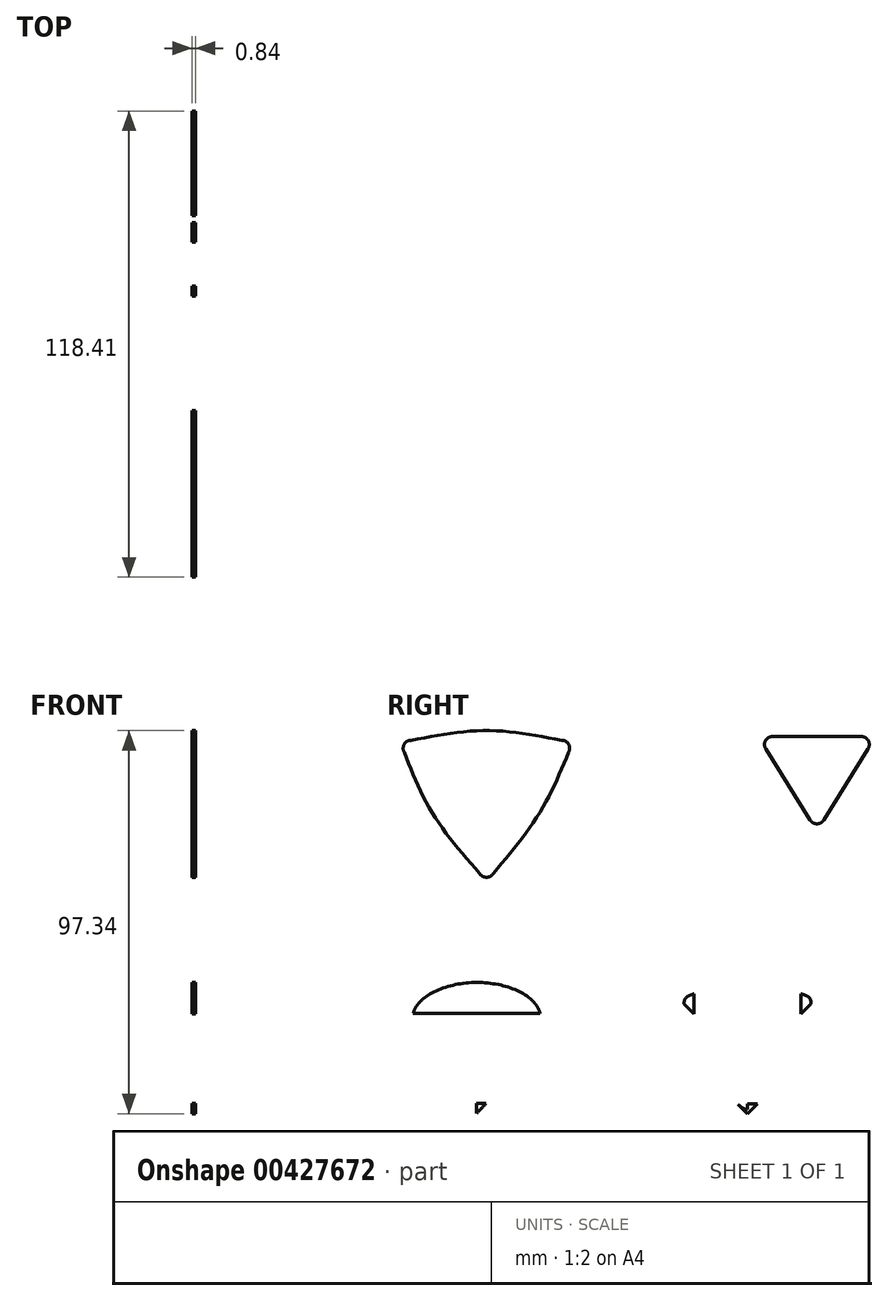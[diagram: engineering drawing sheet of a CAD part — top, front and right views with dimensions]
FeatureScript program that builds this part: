
annotation { "Feature Type Name" : "Feature", "Feature Type Description" : "" }
export const myFeature = defineFeature(function(context is Context, id is Id, definition is map)
    precondition{}
    {
        {
            var Q0;
            Q0=qCreatedBy(makeId("Right.planeOp"),FACE);
            var sketch = newSketch(context, id + "F0", { "sketchPlane" : qUnion([Q0])});
            skLineSegment(sketch, "E0", {"start": v(0, -11.07) * mm, "end": v(0, -44.35) * mm});
            skLineSegment(sketch, "E1", {"start": v(0, -44.35) * mm, "end": v(32.26, -44.35) * mm});
            skPoint(sketch, "E2", {"position": v(16.13, -44.35) * mm});
            skLineSegment(sketch, "E3", {"start": v(0, -11.07) * mm, "end": v(32.26, -11.07) * mm});
            skLineSegment(sketch, "E4", {"start": v(32.26, -11.07) * mm, "end": v(32.26, -44.35) * mm});
            skPoint(sketch, "E5", {"position": v(0, -16.42) * mm});
            skPoint(sketch, "E6", {"position": v(32.26, -16.42) * mm});
            skLineSegment(sketch, "E7", {"start": v(16.13, -44.35) * mm, "end": v(16.13, -39.27) * mm});
            skLineSegment(sketch, "E8", {"start": v(16.13, -41.8) * mm, "end": v(13.59, -41.8) * mm});
            skLineSegment(sketch, "E9", {"start": v(13.59, -41.8) * mm, "end": v(16.13, -41.8) * mm});
            skLineSegment(sketch, "E10", {"start": v(18.67, -41.8) * mm, "end": v(16.13, -41.8) * mm});
            skLineSegment(sketch, "E11", {"start": v(16.13, -44.35) * mm, "end": v(13.59, -41.8) * mm});
            skLineSegment(sketch, "E12", {"start": v(16.13, -44.35) * mm, "end": v(18.67, -41.8) * mm});
            skLineSegment(sketch, "E13", {"start": v(0, -16.42) * mm, "end": v(2.54, -16.42) * mm});
            skLineSegment(sketch, "E14", {"start": v(2.54, -16.42) * mm, "end": v(2.54, -13.88) * mm});
            skLineSegment(sketch, "E15", {"start": v(2.54, -13.88) * mm, "end": v(2.54, -16.42) * mm});
            skLineSegment(sketch, "E16", {"start": v(2.54, -18.96) * mm, "end": v(2.54, -16.42) * mm});
            skLineSegment(sketch, "E17", {"start": v(0, -16.42) * mm, "end": v(2.54, -18.96) * mm});
            skLineSegment(sketch, "E18", {"start": v(2.54, -13.88) * mm, "end": v(0, -16.42) * mm});
            skLineSegment(sketch, "E19", {"start": v(32.26, -16.42) * mm, "end": v(29.72, -16.42) * mm});
            skLineSegment(sketch, "E20", {"start": v(29.72, -16.42) * mm, "end": v(29.72, -13.88) * mm});
            skLineSegment(sketch, "E21", {"start": v(29.72, -13.88) * mm, "end": v(29.72, -16.42) * mm});
            skLineSegment(sketch, "E22", {"start": v(29.72, -18.96) * mm, "end": v(29.72, -16.42) * mm});
            skLineSegment(sketch, "E23", {"start": v(29.72, -18.96) * mm, "end": v(32.26, -16.42) * mm});
            skFitSpline(sketch, "E24", {"points": [v(2.54, -13.88) * mm, v(16.13, -11.07) * mm, v(29.72, -13.88) * mm, v(32.26, -16.42) * mm, v(18.67, -41.8) * mm, v(13.59, -41.8) * mm, v(0, -16.42) * mm, v(2.54, -13.88) * mm]});
            skLineSegment(sketch, "E25", {"start": v(29.72, -13.88) * mm, "end": v(32.26, -16.42) * mm});
            skSolve(sketch);
        }
        {
            var Q0;
            {var subQ0=sQuery(id+"F0.wireOp",EDGE,"E24");var subQ1=sQuery(id+"F0.wireOp",EDGE,"E0");var subQ3=makeQuery(id+"F0.imprint","INTERSECT",VERTEX,{"derivedFrom":[subQ1,subQ0]});Q0=makeQuery(id+"F0.imprint","IMPRINT",FACE,{"disambiguationData":[TD([[makeQuery(id+"F0.imprint","IMPRINT",EDGE,{"disambiguationData":[TD([[subQ3,-1.0]])],"derivedFrom":subQ1}),-1.0]])]});}
            var Q1;
            {var subQ0=sQuery(id+"F0.wireOp",EDGE,"E24");var subQ1=sQuery(id+"F0.wireOp",EDGE,"E4");var subQ3=makeQuery(id+"F0.imprint","INTERSECT",VERTEX,{"derivedFrom":[subQ1,subQ0]});Q1=makeQuery(id+"F0.imprint","IMPRINT",FACE,{"disambiguationData":[TD([[makeQuery(id+"F0.imprint","IMPRINT",EDGE,{"disambiguationData":[TD([[subQ3,-1.0]])],"derivedFrom":subQ1}),1.0]])]});}
            var Q2;
            Q2=makeQuery(id+"F0.imprint","IMPRINT",FACE,{"disambiguationData":[TD([[makeQuery(id+"F0.imprint","IMPRINT",EDGE,{"derivedFrom":sQuery(id+"F0.wireOp",EDGE,"E13")}),-1.0]])]});
            var Q3;
            Q3=makeQuery(id+"F0.imprint","IMPRINT",FACE,{"disambiguationData":[TD([[makeQuery(id+"F0.imprint","IMPRINT",EDGE,{"derivedFrom":sQuery(id+"F0.wireOp",EDGE,"E19")}),1.0]])]});
            var Q4;
            {var subQ1=sQuery(id+"F0.wireOp",EDGE,"E18");Q4=makeQuery(id+"F0.imprint","IMPRINT",FACE,{"disambiguationData":[TD([[makeQuery(id+"F0.imprint","IMPRINT",EDGE,{"derivedFrom":subQ1}),-1.0]])]});}
            var Q5;
            {var subQ0=sQuery(id+"F0.wireOp",EDGE,"E25");Q5=makeQuery(id+"F0.imprint","IMPRINT",FACE,{"disambiguationData":[TD([[makeQuery(id+"F0.imprint","IMPRINT",EDGE,{"derivedFrom":subQ0}),1.0]])]});}
            var Q6;
            {var subQ1=sQuery(id+"F0.wireOp",EDGE,"E7");var subQ3=sQuery(id+"F0.wireOp",EDGE,"E24");var subQ4=makeQuery(id+"F0.imprint","INTERSECT",VERTEX,{"derivedFrom":[subQ1,subQ3]});Q6=makeQuery(id+"F0.imprint","IMPRINT",FACE,{"disambiguationData":[TD([[makeQuery(id+"F0.imprint","IMPRINT",EDGE,{"disambiguationData":[TD([[subQ4,-1.0]])],"derivedFrom":subQ3}),1.0]])]});}
            var Q7;
            {var subQ1=sQuery(id+"F0.wireOp",EDGE,"E7");var subQ3=sQuery(id+"F0.wireOp",EDGE,"E24");var subQ4=makeQuery(id+"F0.imprint","INTERSECT",VERTEX,{"derivedFrom":[subQ1,subQ3]});Q7=makeQuery(id+"F0.imprint","IMPRINT",FACE,{"disambiguationData":[TD([[makeQuery(id+"F0.imprint","IMPRINT",EDGE,{"disambiguationData":[TD([[subQ4,1.0]])],"derivedFrom":subQ3}),1.0]])]});}
            var Q8;
            Q8=makeQuery(id+"F0.imprint","IMPRINT",FACE,{"disambiguationData":[TD([[makeQuery(id+"F0.imprint","IMPRINT",EDGE,{"derivedFrom":sQuery(id+"F0.wireOp",EDGE,"E13")}),1.0]])]});
            var Q9;
            Q9=makeQuery(id+"F0.imprint","IMPRINT",FACE,{"disambiguationData":[TD([[makeQuery(id+"F0.imprint","IMPRINT",EDGE,{"derivedFrom":sQuery(id+"F0.wireOp",EDGE,"E19")}),-1.0]])]});
            var Q10;
            {var subQ8=sQuery(id+"F0.wireOp",EDGE,"E9");Q10=makeQuery(id+"F0.imprint","IMPRINT",FACE,{"disambiguationData":[TD([[makeQuery(id+"F0.imprint","IMPRINT",EDGE,{"derivedFrom":subQ8}),1.0]])]});}
            var Q11;
            {var subQ0=sQuery(id+"F0.wireOp",EDGE,"E9");Q11=makeQuery(id+"F0.imprint","IMPRINT",FACE,{"disambiguationData":[TD([[makeQuery(id+"F0.imprint","IMPRINT",EDGE,{"derivedFrom":subQ0}),-1.0]])]});}
            var Q12;
            {var subQ0=sQuery(id+"F0.wireOp",EDGE,"E10");Q12=makeQuery(id+"F0.imprint","IMPRINT",FACE,{"disambiguationData":[TD([[makeQuery(id+"F0.imprint","IMPRINT",EDGE,{"derivedFrom":subQ0}),1.0]])]});}
            extrude(context, id + "F1", {"entities" : qUnion([Q0, Q1, Q2, Q3, Q4, Q5, Q6, Q7, Q8, Q9, Q10, Q11, Q12]), "depth" : 0.84 * mm});
        }
        {
            var Q0;
            Q0=qCreatedBy(makeId("Right.planeOp"),FACE);
            var sketch = newSketch(context, id + "F2", { "sketchPlane" : qUnion([Q0])});
            skLineSegment(sketch, "E26", {"start": v(-68.83, -11.02) * mm, "end": v(-68.83, -44.3) * mm});
            skLineSegment(sketch, "E27", {"start": v(-68.83, -44.3) * mm, "end": v(-36.58, -44.3) * mm});
            skPoint(sketch, "E28", {"position": v(-52.7, -44.3) * mm});
            skLineSegment(sketch, "E29", {"start": v(-68.83, -11.02) * mm, "end": v(-36.58, -11.02) * mm});
            skLineSegment(sketch, "E30", {"start": v(-36.58, -11.02) * mm, "end": v(-36.58, -44.3) * mm});
            skPoint(sketch, "E31", {"position": v(-68.83, -16.36) * mm});
            skPoint(sketch, "E32", {"position": v(-36.58, -16.36) * mm});
            skLineSegment(sketch, "E33", {"start": v(-52.7, -44.3) * mm, "end": v(-52.7, -39.21) * mm});
            skLineSegment(sketch, "E34", {"start": v(-52.7, -41.75) * mm, "end": v(-55.24, -41.75) * mm});
            skLineSegment(sketch, "E35", {"start": v(-55.24, -41.75) * mm, "end": v(-52.7, -41.75) * mm});
            skLineSegment(sketch, "E36", {"start": v(-50.16, -41.75) * mm, "end": v(-52.7, -41.75) * mm});
            skLineSegment(sketch, "E37", {"start": v(-52.7, -44.3) * mm, "end": v(-55.24, -41.75) * mm});
            skLineSegment(sketch, "E38", {"start": v(-52.7, -44.3) * mm, "end": v(-50.16, -41.75) * mm});
            skLineSegment(sketch, "E39", {"start": v(-68.83, -16.36) * mm, "end": v(-66.3, -16.36) * mm});
            skLineSegment(sketch, "E40", {"start": v(-66.3, -16.36) * mm, "end": v(-66.3, -13.82) * mm});
            skLineSegment(sketch, "E41", {"start": v(-66.3, -13.82) * mm, "end": v(-66.3, -16.36) * mm});
            skLineSegment(sketch, "E42", {"start": v(-66.3, -18.9) * mm, "end": v(-66.3, -16.36) * mm});
            skLineSegment(sketch, "E43", {"start": v(-68.83, -16.36) * mm, "end": v(-66.3, -18.9) * mm});
            skLineSegment(sketch, "E44", {"start": v(-66.3, -13.82) * mm, "end": v(-68.83, -16.36) * mm});
            skLineSegment(sketch, "E45", {"start": v(-36.58, -16.36) * mm, "end": v(-39.12, -16.36) * mm});
            skLineSegment(sketch, "E46", {"start": v(-39.12, -16.36) * mm, "end": v(-39.12, -13.82) * mm});
            skLineSegment(sketch, "E47", {"start": v(-39.12, -13.82) * mm, "end": v(-39.12, -16.36) * mm});
            skLineSegment(sketch, "E48", {"start": v(-39.12, -18.9) * mm, "end": v(-39.12, -16.36) * mm});
            skLineSegment(sketch, "E49", {"start": v(-39.12, -18.9) * mm, "end": v(-36.58, -16.36) * mm});
            skLineSegment(sketch, "E50", {"start": v(-39.12, -13.82) * mm, "end": v(-36.58, -16.36) * mm});
            skLineSegment(sketch, "E51", {"start": v(-66.3, -18.9) * mm, "end": v(-68.83, -18.9) * mm});
            skLineSegment(sketch, "E52", {"start": v(-68.83, -18.9) * mm, "end": v(-36.58, -18.9) * mm});
            skFitSpline(sketch, "E53", {"points": [v(-55.24, -41.75) * mm, v(-68.83, -18.9) * mm, v(-52.7, -11.02) * mm, v(-36.58, -18.9) * mm, v(-52.7, -44.3) * mm], "startDerivative": vector(-84.15, 94.44) * mm, "endDerivative": vector(-92.62, -99.56) * mm});
            skSolve(sketch);
        }
        {
            var Q0;
            {var subQ0=sQuery(id+"F2.wireOp",EDGE,"E35");Q0=makeQuery(id+"F2.imprint","IMPRINT",FACE,{"disambiguationData":[TD([[makeQuery(id+"F2.imprint","IMPRINT",EDGE,{"derivedFrom":subQ0}),1.0]])]});}
            var Q1;
            {var subQ4=sQuery(id+"F2.wireOp",EDGE,"E42");Q1=makeQuery(id+"F2.imprint","IMPRINT",FACE,{"disambiguationData":[TD([[makeQuery(id+"F2.imprint","IMPRINT",EDGE,{"derivedFrom":subQ4}),-1.0]])]});}
            var Q2;
            {var subQ1=sQuery(id+"F2.wireOp",EDGE,"E43");var subQ3=sQuery(id+"F2.wireOp",EDGE,"E53");var subQ4=makeQuery(id+"F2.imprint","INTERSECT",VERTEX,{"derivedFrom":[subQ1,subQ3]});Q2=makeQuery(id+"F2.imprint","IMPRINT",FACE,{"disambiguationData":[TD([[makeQuery(id+"F2.imprint","IMPRINT",EDGE,{"disambiguationData":[TD([[subQ4,-1.0]])],"derivedFrom":subQ1}),-1.0]])]});}
            var Q3;
            {var subQ0=sQuery(id+"F2.wireOp",EDGE,"E42");Q3=makeQuery(id+"F2.imprint","IMPRINT",FACE,{"disambiguationData":[TD([[makeQuery(id+"F2.imprint","IMPRINT",EDGE,{"derivedFrom":subQ0}),1.0]])]});}
            var Q4;
            {var subQ1=sQuery(id+"F2.wireOp",EDGE,"E39");var subQ3=sQuery(id+"F2.wireOp",EDGE,"E53");var subQ4=makeQuery(id+"F2.imprint","INTERSECT",VERTEX,{"derivedFrom":[subQ1,subQ3]});Q4=makeQuery(id+"F2.imprint","IMPRINT",FACE,{"disambiguationData":[TD([[makeQuery(id+"F2.imprint","IMPRINT",EDGE,{"disambiguationData":[TD([[subQ4,-1.0]])],"derivedFrom":subQ3}),-1.0]])]});}
            var Q5;
            {var subQ1=sQuery(id+"F2.wireOp",EDGE,"E49");var subQ3=sQuery(id+"F2.wireOp",EDGE,"E53");var subQ4=makeQuery(id+"F2.imprint","INTERSECT",VERTEX,{"derivedFrom":[subQ1,subQ3]});Q5=makeQuery(id+"F2.imprint","IMPRINT",FACE,{"disambiguationData":[TD([[makeQuery(id+"F2.imprint","IMPRINT",EDGE,{"disambiguationData":[TD([[subQ4,1.0]])],"derivedFrom":subQ1}),-1.0]])]});}
            var Q6;
            {var subQ0=sQuery(id+"F2.wireOp",EDGE,"E48");Q6=makeQuery(id+"F2.imprint","IMPRINT",FACE,{"disambiguationData":[TD([[makeQuery(id+"F2.imprint","IMPRINT",EDGE,{"derivedFrom":subQ0}),-1.0]])]});}
            var Q7;
            {var subQ0=sQuery(id+"F2.wireOp",EDGE,"E53");var subQ3=sQuery(id+"F2.wireOp",EDGE,"E36");var subQ5=makeQuery(id+"F2.imprint","INTERSECT",VERTEX,{"derivedFrom":[subQ3,subQ0]});Q7=makeQuery(id+"F2.imprint","IMPRINT",FACE,{"disambiguationData":[TD([[makeQuery(id+"F2.imprint","IMPRINT",EDGE,{"disambiguationData":[TD([[subQ5,-1.0]])],"derivedFrom":subQ3}),1.0]])]});}
            var Q8;
            {var subQ2=sQuery(id+"F2.wireOp",EDGE,"E35");Q8=makeQuery(id+"F2.imprint","IMPRINT",FACE,{"disambiguationData":[TD([[makeQuery(id+"F2.imprint","IMPRINT",EDGE,{"derivedFrom":subQ2}),-1.0]])]});}
            var Q9;
            {var subQ1=sQuery(id+"F2.wireOp",EDGE,"E45");var subQ3=sQuery(id+"F2.wireOp",EDGE,"E53");var subQ4=makeQuery(id+"F2.imprint","INTERSECT",VERTEX,{"derivedFrom":[subQ1,subQ3]});Q9=makeQuery(id+"F2.imprint","IMPRINT",FACE,{"disambiguationData":[TD([[makeQuery(id+"F2.imprint","IMPRINT",EDGE,{"disambiguationData":[TD([[subQ4,1.0]])],"derivedFrom":subQ3}),-1.0]])]});}
            extrude(context, id + "F3", {"entities" : qUnion([Q0, Q1, Q2, Q3, Q4, Q5, Q6, Q7, Q8, Q9]), "depth" : 0.84 * mm});
        }
        {
            var Q0;
            Q0=qCreatedBy(makeId("Right.planeOp"),FACE);
            var sketch = newSketch(context, id + "F4", { "sketchPlane" : qUnion([Q0])});
            skCircle(sketch, "E54", {"center": v(33.74, 44.11) * mm, "radius": 16.64 * mm});
            skLineSegment(sketch, "E55", {"start": v(18.82, 51.46) * mm, "end": v(33.74, 27.47) * mm});
            skLineSegment(sketch, "E56", {"start": v(33.74, 27.47) * mm, "end": v(48.67, 51.46) * mm});
            skLineSegment(sketch, "E57", {"start": v(48.67, 51.46) * mm, "end": v(18.82, 51.46) * mm});
            skSolve(sketch);
        }
        {
            var Q0;
            Q0=makeQuery(id+"F4.imprint","IMPRINT",FACE,{"disambiguationData":[TD([[makeQuery(id+"F4.imprint","IMPRINT",EDGE,{"derivedFrom":sQuery(id+"F4.wireOp",EDGE,"E55")}),1.0]])]});
            extrude(context, id + "F5", {"entities" : qUnion([Q0]), "depth" : 0.84 * mm});
        }
        {
            var Q0;
            Q0=makeQuery(id+"F5.opExtrude","SWEPT_EDGE",EDGE,{"disambiguationData":[OSD([sQuery(id+"F4.wireOp",EDGE,"E54"),sQuery(id+"F4.wireOp",EDGE,"E55"),sQuery(id+"F4.wireOp",EDGE,"E57")])]});
            var Q1;
            Q1=makeQuery(id+"F5.opExtrude","SWEPT_EDGE",EDGE,{"disambiguationData":[OSD([sQuery(id+"F4.wireOp",EDGE,"E54"),sQuery(id+"F4.wireOp",EDGE,"E55"),sQuery(id+"F4.wireOp",EDGE,"E56")])]});
            var Q2;
            Q2=makeQuery(id+"F5.opExtrude","SWEPT_EDGE",EDGE,{"disambiguationData":[OSD([sQuery(id+"F4.wireOp",EDGE,"E54"),sQuery(id+"F4.wireOp",EDGE,"E56"),sQuery(id+"F4.wireOp",EDGE,"E57")])]});
            fillet(context, id + "F6", {"entities" : qUnion([Q0, Q1, Q2]), "radius" : 2.03 * mm, "tangentPropagation" : true, "allowEdgeOverflow" : false});
        }
        {
            var Q0;
            Q0=qCreatedBy(makeId("Right.planeOp"),FACE);
            var sketch = newSketch(context, id + "F7", { "sketchPlane" : qUnion([Q0])});
            skCircle(sketch, "E58", {"center": v(-50.21, 39.29) * mm, "radius": 25.4 * mm});
            skLineSegment(sketch, "E59", {"start": v(-73, 50.52) * mm, "end": v(-50.21, 13.89) * mm});
            skLineSegment(sketch, "E60", {"start": v(-50.21, 13.89) * mm, "end": v(-27.43, 50.52) * mm});
            skLineSegment(sketch, "E61", {"start": v(-27.43, 50.52) * mm, "end": v(-73, 50.52) * mm});
            skSolve(sketch);
        }
        {
            var Q0;
            Q0=makeQuery(id+"F7.imprint","IMPRINT",FACE,{"disambiguationData":[TD([[makeQuery(id+"F7.imprint","IMPRINT",EDGE,{"derivedFrom":sQuery(id+"F7.wireOp",EDGE,"E59")}),1.0]])]});
            extrude(context, id + "F8", {"entities" : qUnion([Q0]), "depth" : 0.84 * mm});
        }
        {
            var Q0;
            Q0=makeQuery(id+"F8.opExtrude","SWEPT_EDGE",EDGE,{"disambiguationData":[OSD([sQuery(id+"F7.wireOp",EDGE,"E58"),sQuery(id+"F7.wireOp",EDGE,"E59"),sQuery(id+"F7.wireOp",EDGE,"E61")])]});
            var Q1;
            Q1=makeQuery(id+"F8.opExtrude","SWEPT_EDGE",EDGE,{"disambiguationData":[OSD([sQuery(id+"F7.wireOp",EDGE,"E58"),sQuery(id+"F7.wireOp",EDGE,"E60"),sQuery(id+"F7.wireOp",EDGE,"E61")])]});
            var Q2;
            Q2=makeQuery(id+"F8.opExtrude","SWEPT_EDGE",EDGE,{"disambiguationData":[OSD([sQuery(id+"F7.wireOp",EDGE,"E58"),sQuery(id+"F7.wireOp",EDGE,"E59"),sQuery(id+"F7.wireOp",EDGE,"E60")])]});
            fillet(context, id + "F9", {"entities" : qUnion([Q0, Q1, Q2]), "radius" : 2.03 * mm, "tangentPropagation" : true, "allowEdgeOverflow" : false});
        }
        {
            var Q0;
            Q0=makeQuery(id+"F8.opExtrude","CAP_FACE",FACE,{"disambiguationData":[OSD([sQuery(id+"F7.wireOp",EDGE,"E59"),sQuery(id+"F7.wireOp",EDGE,"E60"),sQuery(id+"F7.wireOp",EDGE,"E61")])],"isStart":false});
            var sketch = newSketch(context, id + "F10", { "sketchPlane" : qUnion([Q0])});
            skPoint(sketch, "E62.1.internal.snap0", {"position": v(-50.21, 50.52) * mm});
            skFitSpline(sketch, "E62", {"points": [v(-69.34, 50.52) * mm, v(-50.21, 52.99) * mm, v(-31.09, 50.52) * mm], "startDerivative": vector(38.25, 7.42) * mm, "endDerivative": vector(38.25, -7.42) * mm});
            skPoint(sketch, "E63.1.internal.snap0", {"position": v(-38.93, 32.04) * mm});
            skFitSpline(sketch, "E63", {"points": [v(-29.36, 47.41) * mm, v(-36.73, 32.04) * mm, v(-48.49, 16.66) * mm], "startDerivative": vector(-13.4, -32.23) * mm, "endDerivative": vector(-24.74, -29.3) * mm});
            skPoint(sketch, "E64.1.internal.snap0", {"position": v(-61.5, 32.04) * mm});
            skFitSpline(sketch, "E64", {"points": [v(-51.94, 16.66) * mm, v(-63.97, 32.04) * mm, v(-71.07, 47.41) * mm], "startDerivative": vector(-25.43, 29.13) * mm, "endDerivative": vector(-12.67, 32.4) * mm});
            skSolve(sketch);
        }
        {
            var Q0;
            Q0 = qSketchRegion(id + "F10", true);
            var Q1;
            Q1=makeQuery(id+"F10.imprint","IMPRINT",FACE,{"disambiguationData":[TD([[makeQuery(id+"F10.imprint","IMPRINT",EDGE,{"derivedFrom":sQuery(id+"F10.wireOp",EDGE,"E64")}),-1.0]])]});
            var Q2;
            Q2=makeQuery(id+"F10.imprint","IMPRINT",FACE,{"disambiguationData":[TD([[makeQuery(id+"F10.imprint","IMPRINT",EDGE,{"derivedFrom":sQuery(id+"F10.wireOp",EDGE,"E63")}),-1.0]])]});
            var Q3;
            Q3=makeQuery(id+"F10.imprint","IMPRINT",FACE,{"disambiguationData":[TD([[makeQuery(id+"F10.imprint","IMPRINT",EDGE,{"derivedFrom":sQuery(id+"F10.wireOp",EDGE,"E62")}),-1.0]])]});
            extrude(context, id + "F11", {"entities" : qUnion([Q0, Q1, Q2, Q3]), "operationType" : NewBodyOperationType.ADD, "oppositeDirection" : true, "depth" : 0.84 * mm});
        }
    });
